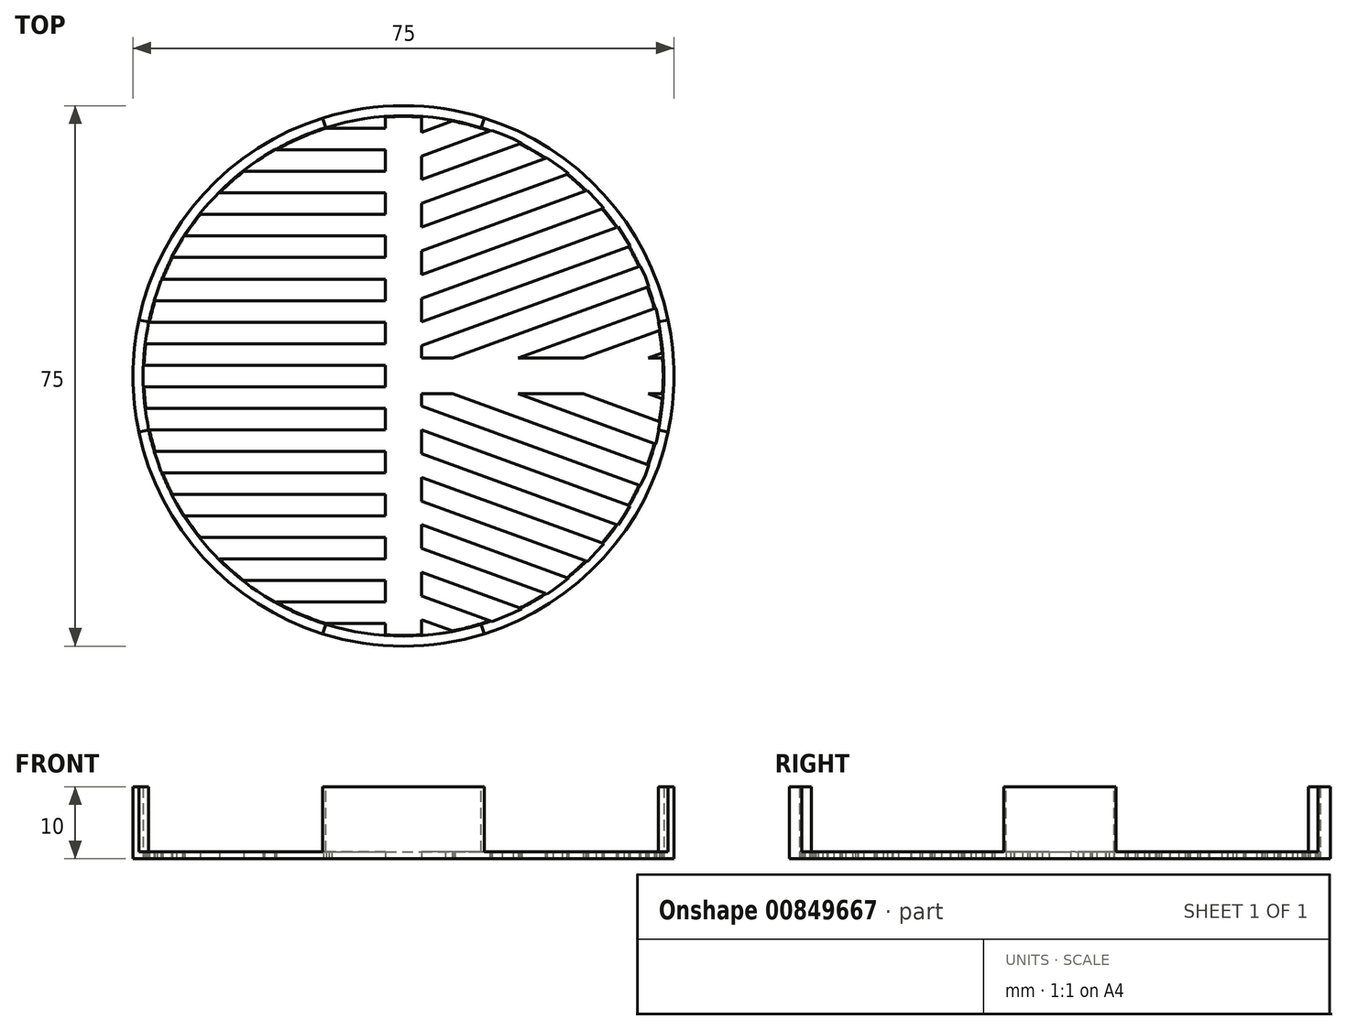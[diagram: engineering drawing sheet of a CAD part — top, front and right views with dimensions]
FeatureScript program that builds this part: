
annotation { "Feature Type Name" : "Feature", "Feature Type Description" : "" }
export const myFeature = defineFeature(function(context is Context, id is Id, definition is map)
    precondition{}
    {
        {
            var Q0;
            Q0=qCreatedBy(makeId("Top.planeOp"),FACE);
            var sketch = newSketch(context, id + "F0", { "sketchPlane" : qUnion([Q0])});
            skLineSegment(sketch, "E0", {"start": v(-11.08, -34.36) * mm, "end": v(-10.31, -34.61) * mm});
            skLineSegment(sketch, "E1", {"start": v(-10.31, -34.61) * mm, "end": v(-7.06, -35.42) * mm});
            skLineSegment(sketch, "E2", {"start": v(-7.06, -35.42) * mm, "end": v(-3.7, -35.92) * mm});
            skLineSegment(sketch, "E3", {"start": v(-3.7, -35.92) * mm, "end": v(-2.5, -36) * mm});
            skLineSegment(sketch, "E4", {"start": v(-2.5, -36) * mm, "end": v(-2.5, -34.36) * mm});
            skLineSegment(sketch, "E5", {"start": v(-2.5, -34.36) * mm, "end": v(-11.08, -34.36) * mm});
            skLineSegment(sketch, "E6", {"start": v(2.5, -33.81) * mm, "end": v(2.5, -36.1) * mm});
            skLineSegment(sketch, "E7", {"start": v(2.5, -36.1) * mm, "end": v(5.83, -35.73) * mm});
            skLineSegment(sketch, "E8", {"start": v(5.83, -35.73) * mm, "end": v(7.1, -35.5) * mm});
            skLineSegment(sketch, "E9", {"start": v(7.1, -35.5) * mm, "end": v(2.5, -33.81) * mm});
            skLineSegment(sketch, "E10", {"start": v(-22.3, -28.39) * mm, "end": v(-21.95, -28.67) * mm});
            skLineSegment(sketch, "E11", {"start": v(-21.95, -28.67) * mm, "end": v(-19.28, -30.53) * mm});
            skLineSegment(sketch, "E12", {"start": v(-19.28, -30.53) * mm, "end": v(-17.88, -31.37) * mm});
            skLineSegment(sketch, "E13", {"start": v(-17.88, -31.37) * mm, "end": v(-2.5, -31.37) * mm});
            skLineSegment(sketch, "E14", {"start": v(-2.5, -31.37) * mm, "end": v(-2.5, -28.39) * mm});
            skLineSegment(sketch, "E15", {"start": v(-2.5, -28.39) * mm, "end": v(-22.3, -28.39) * mm});
            skLineSegment(sketch, "E16", {"start": v(2.5, -27.23) * mm, "end": v(2.5, -30.52) * mm});
            skLineSegment(sketch, "E17", {"start": v(2.5, -30.52) * mm, "end": v(12.26, -34.08) * mm});
            skLineSegment(sketch, "E18", {"start": v(12.26, -34.08) * mm, "end": v(13.7, -33.52) * mm});
            skLineSegment(sketch, "E19", {"start": v(13.7, -33.52) * mm, "end": v(15.18, -32.88) * mm});
            skLineSegment(sketch, "E20", {"start": v(15.18, -32.88) * mm, "end": v(16.4, -32.3) * mm});
            skLineSegment(sketch, "E21", {"start": v(16.4, -32.3) * mm, "end": v(2.5, -27.23) * mm});
            skLineSegment(sketch, "E22", {"start": v(-28.3, -22.41) * mm, "end": v(-27.8, -23.05) * mm});
            skLineSegment(sketch, "E23", {"start": v(-27.8, -23.05) * mm, "end": v(-26.73, -24.28) * mm});
            skLineSegment(sketch, "E24", {"start": v(-26.73, -24.28) * mm, "end": v(-25.66, -25.4) * mm});
            skLineSegment(sketch, "E25", {"start": v(-25.66, -25.4) * mm, "end": v(-2.5, -25.4) * mm});
            skLineSegment(sketch, "E26", {"start": v(-2.5, -25.4) * mm, "end": v(-2.5, -22.41) * mm});
            skLineSegment(sketch, "E27", {"start": v(-2.5, -22.41) * mm, "end": v(-28.3, -22.41) * mm});
            skLineSegment(sketch, "E28", {"start": v(2.5, -20.65) * mm, "end": v(2.5, -23.94) * mm});
            skLineSegment(sketch, "E29", {"start": v(2.5, -23.94) * mm, "end": v(19.88, -30.27) * mm});
            skLineSegment(sketch, "E30", {"start": v(19.88, -30.27) * mm, "end": v(20.74, -29.7) * mm});
            skLineSegment(sketch, "E31", {"start": v(20.74, -29.7) * mm, "end": v(22.02, -28.76) * mm});
            skLineSegment(sketch, "E32", {"start": v(22.02, -28.76) * mm, "end": v(22.88, -28.07) * mm});
            skLineSegment(sketch, "E33", {"start": v(22.88, -28.07) * mm, "end": v(2.5, -20.65) * mm});
            skLineSegment(sketch, "E34", {"start": v(-32.15, -16.43) * mm, "end": v(-31.48, -17.69) * mm});
            skLineSegment(sketch, "E35", {"start": v(-31.48, -17.69) * mm, "end": v(-30.65, -19.1) * mm});
            skLineSegment(sketch, "E36", {"start": v(-30.65, -19.1) * mm, "end": v(-30.43, -19.42) * mm});
            skLineSegment(sketch, "E37", {"start": v(-30.43, -19.42) * mm, "end": v(-2.5, -19.42) * mm});
            skLineSegment(sketch, "E38", {"start": v(-2.5, -19.42) * mm, "end": v(-2.5, -16.43) * mm});
            skLineSegment(sketch, "E39", {"start": v(-2.5, -16.43) * mm, "end": v(-32.15, -16.43) * mm});
            skLineSegment(sketch, "E40", {"start": v(2.5, -14.07) * mm, "end": v(2.5, -17.36) * mm});
            skLineSegment(sketch, "E41", {"start": v(2.5, -17.36) * mm, "end": v(25.49, -25.73) * mm});
            skLineSegment(sketch, "E42", {"start": v(25.49, -25.73) * mm, "end": v(25.61, -25.61) * mm});
            skLineSegment(sketch, "E43", {"start": v(25.61, -25.61) * mm, "end": v(26.7, -24.46) * mm});
            skLineSegment(sketch, "E44", {"start": v(26.7, -24.46) * mm, "end": v(27.76, -23.27) * mm});
            skLineSegment(sketch, "E45", {"start": v(27.76, -23.27) * mm, "end": v(2.5, -14.07) * mm});
            skLineSegment(sketch, "E46", {"start": v(-34.56, -10.46) * mm, "end": v(-34.17, -11.68) * mm});
            skLineSegment(sketch, "E47", {"start": v(-34.17, -11.68) * mm, "end": v(-33.6, -13.24) * mm});
            skLineSegment(sketch, "E48", {"start": v(-33.6, -13.24) * mm, "end": v(-33.51, -13.45) * mm});
            skLineSegment(sketch, "E49", {"start": v(-33.51, -13.45) * mm, "end": v(-2.5, -13.45) * mm});
            skLineSegment(sketch, "E50", {"start": v(-2.5, -13.45) * mm, "end": v(-2.5, -10.46) * mm});
            skLineSegment(sketch, "E51", {"start": v(-2.5, -10.46) * mm, "end": v(-34.56, -10.46) * mm});
            skLineSegment(sketch, "E52", {"start": v(2.5, -7.49) * mm, "end": v(2.5, -10.78) * mm});
            skLineSegment(sketch, "E53", {"start": v(2.5, -10.78) * mm, "end": v(29.73, -20.7) * mm});
            skLineSegment(sketch, "E54", {"start": v(29.73, -20.7) * mm, "end": v(30.58, -19.4) * mm});
            skLineSegment(sketch, "E55", {"start": v(30.58, -19.4) * mm, "end": v(31.4, -18.04) * mm});
            skLineSegment(sketch, "E56", {"start": v(31.4, -18.04) * mm, "end": v(31.42, -18.02) * mm});
            skLineSegment(sketch, "E57", {"start": v(31.42, -18.02) * mm, "end": v(2.5, -7.49) * mm});
            skLineSegment(sketch, "E58", {"start": v(-35.82, -4.48) * mm, "end": v(-35.74, -5.16) * mm});
            skLineSegment(sketch, "E59", {"start": v(-35.74, -5.16) * mm, "end": v(-35.46, -6.83) * mm});
            skLineSegment(sketch, "E60", {"start": v(-35.46, -6.83) * mm, "end": v(-35.32, -7.47) * mm});
            skLineSegment(sketch, "E61", {"start": v(-35.32, -7.47) * mm, "end": v(-2.5, -7.47) * mm});
            skLineSegment(sketch, "E62", {"start": v(-2.5, -7.47) * mm, "end": v(-2.5, -4.48) * mm});
            skLineSegment(sketch, "E63", {"start": v(-2.5, -4.48) * mm, "end": v(-35.82, -4.48) * mm});
            skLineSegment(sketch, "E64", {"start": v(33.96, -2.5) * mm, "end": v(36.04, -3.24) * mm});
            skLineSegment(sketch, "E65", {"start": v(36.04, -3.24) * mm, "end": v(36.1, -2.5) * mm});
            skLineSegment(sketch, "E66", {"start": v(36.1, -2.5) * mm, "end": v(33.96, -2.5) * mm});
            skLineSegment(sketch, "E67", {"start": v(15.88, -2.5) * mm, "end": v(34.95, -9.43) * mm});
            skLineSegment(sketch, "E68", {"start": v(34.95, -9.43) * mm, "end": v(35.06, -9.07) * mm});
            skLineSegment(sketch, "E69", {"start": v(35.06, -9.07) * mm, "end": v(35.43, -7.46) * mm});
            skLineSegment(sketch, "E70", {"start": v(35.43, -7.46) * mm, "end": v(35.62, -6.38) * mm});
            skLineSegment(sketch, "E71", {"start": v(35.62, -6.38) * mm, "end": v(24.92, -2.5) * mm});
            skLineSegment(sketch, "E72", {"start": v(24.92, -2.5) * mm, "end": v(15.88, -2.5) * mm});
            skLineSegment(sketch, "E73", {"start": v(2.5, -2.5) * mm, "end": v(2.5, -4.2) * mm});
            skLineSegment(sketch, "E74", {"start": v(2.5, -4.2) * mm, "end": v(32.85, -15.25) * mm});
            skLineSegment(sketch, "E75", {"start": v(32.85, -15.25) * mm, "end": v(32.88, -15.18) * mm});
            skLineSegment(sketch, "E76", {"start": v(32.88, -15.18) * mm, "end": v(33.52, -13.7) * mm});
            skLineSegment(sketch, "E77", {"start": v(33.52, -13.7) * mm, "end": v(34.03, -12.38) * mm});
            skLineSegment(sketch, "E78", {"start": v(34.03, -12.38) * mm, "end": v(6.84, -2.5) * mm});
            skLineSegment(sketch, "E79", {"start": v(6.84, -2.5) * mm, "end": v(2.5, -2.5) * mm});
            skLineSegment(sketch, "E80", {"start": v(-36.07, 1.5) * mm, "end": v(-36.1, 0) * mm});
            skLineSegment(sketch, "E81", {"start": v(-36.1, 0) * mm, "end": v(-36.07, -1.5) * mm});
            skLineSegment(sketch, "E82", {"start": v(-36.07, -1.5) * mm, "end": v(-2.5, -1.5) * mm});
            skLineSegment(sketch, "E83", {"start": v(-2.5, -1.5) * mm, "end": v(-2.5, 1.5) * mm});
            skLineSegment(sketch, "E84", {"start": v(-2.5, 1.5) * mm, "end": v(-36.07, 1.5) * mm});
            skLineSegment(sketch, "E85", {"start": v(36.04, 3.25) * mm, "end": v(33.96, 2.5) * mm});
            skLineSegment(sketch, "E86", {"start": v(33.96, 2.5) * mm, "end": v(36.1, 2.5) * mm});
            skLineSegment(sketch, "E87", {"start": v(36.1, 2.5) * mm, "end": v(36.04, 3.25) * mm});
            skLineSegment(sketch, "E88", {"start": v(-35.32, 7.47) * mm, "end": v(-35.46, 6.84) * mm});
            skLineSegment(sketch, "E89", {"start": v(-35.46, 6.84) * mm, "end": v(-35.74, 5.16) * mm});
            skLineSegment(sketch, "E90", {"start": v(-35.74, 5.16) * mm, "end": v(-35.82, 4.48) * mm});
            skLineSegment(sketch, "E91", {"start": v(-35.82, 4.48) * mm, "end": v(-2.5, 4.48) * mm});
            skLineSegment(sketch, "E92", {"start": v(-2.5, 4.48) * mm, "end": v(-2.5, 7.47) * mm});
            skLineSegment(sketch, "E93", {"start": v(-2.5, 7.47) * mm, "end": v(-35.32, 7.47) * mm});
            skLineSegment(sketch, "E94", {"start": v(34.95, 9.43) * mm, "end": v(15.88, 2.5) * mm});
            skLineSegment(sketch, "E95", {"start": v(15.88, 2.5) * mm, "end": v(24.92, 2.5) * mm});
            skLineSegment(sketch, "E96", {"start": v(24.92, 2.5) * mm, "end": v(35.62, 6.39) * mm});
            skLineSegment(sketch, "E97", {"start": v(35.62, 6.39) * mm, "end": v(35.43, 7.46) * mm});
            skLineSegment(sketch, "E98", {"start": v(35.43, 7.46) * mm, "end": v(35.06, 9.07) * mm});
            skLineSegment(sketch, "E99", {"start": v(35.06, 9.07) * mm, "end": v(34.95, 9.43) * mm});
            skLineSegment(sketch, "E100", {"start": v(-33.51, 13.45) * mm, "end": v(-33.6, 13.24) * mm});
            skLineSegment(sketch, "E101", {"start": v(-33.6, 13.24) * mm, "end": v(-34.17, 11.68) * mm});
            skLineSegment(sketch, "E102", {"start": v(-34.17, 11.68) * mm, "end": v(-34.56, 10.46) * mm});
            skLineSegment(sketch, "E103", {"start": v(-34.56, 10.46) * mm, "end": v(-2.5, 10.46) * mm});
            skLineSegment(sketch, "E104", {"start": v(-2.5, 10.46) * mm, "end": v(-2.5, 13.45) * mm});
            skLineSegment(sketch, "E105", {"start": v(-2.5, 13.45) * mm, "end": v(-33.51, 13.45) * mm});
            skLineSegment(sketch, "E106", {"start": v(32.85, 15.25) * mm, "end": v(2.5, 4.2) * mm});
            skLineSegment(sketch, "E107", {"start": v(2.5, 4.2) * mm, "end": v(2.5, 2.5) * mm});
            skLineSegment(sketch, "E108", {"start": v(2.5, 2.5) * mm, "end": v(6.84, 2.5) * mm});
            skLineSegment(sketch, "E109", {"start": v(6.84, 2.5) * mm, "end": v(34.03, 12.38) * mm});
            skLineSegment(sketch, "E110", {"start": v(34.03, 12.38) * mm, "end": v(33.52, 13.7) * mm});
            skLineSegment(sketch, "E111", {"start": v(33.52, 13.7) * mm, "end": v(32.88, 15.18) * mm});
            skLineSegment(sketch, "E112", {"start": v(32.88, 15.18) * mm, "end": v(32.85, 15.25) * mm});
            skLineSegment(sketch, "E113", {"start": v(-30.43, 19.42) * mm, "end": v(-30.65, 19.1) * mm});
            skLineSegment(sketch, "E114", {"start": v(-30.65, 19.1) * mm, "end": v(-31.48, 17.69) * mm});
            skLineSegment(sketch, "E115", {"start": v(-31.48, 17.69) * mm, "end": v(-32.15, 16.43) * mm});
            skLineSegment(sketch, "E116", {"start": v(-32.15, 16.43) * mm, "end": v(-2.5, 16.43) * mm});
            skLineSegment(sketch, "E117", {"start": v(-2.5, 16.43) * mm, "end": v(-2.5, 19.42) * mm});
            skLineSegment(sketch, "E118", {"start": v(-2.5, 19.42) * mm, "end": v(-30.43, 19.42) * mm});
            skLineSegment(sketch, "E119", {"start": v(29.73, 20.7) * mm, "end": v(2.5, 10.78) * mm});
            skLineSegment(sketch, "E120", {"start": v(2.5, 10.78) * mm, "end": v(2.5, 7.49) * mm});
            skLineSegment(sketch, "E121", {"start": v(2.5, 7.49) * mm, "end": v(31.42, 18.02) * mm});
            skLineSegment(sketch, "E122", {"start": v(31.42, 18.02) * mm, "end": v(31.4, 18.04) * mm});
            skLineSegment(sketch, "E123", {"start": v(31.4, 18.04) * mm, "end": v(30.58, 19.4) * mm});
            skLineSegment(sketch, "E124", {"start": v(30.58, 19.4) * mm, "end": v(29.73, 20.7) * mm});
            skLineSegment(sketch, "E125", {"start": v(-25.66, 25.4) * mm, "end": v(-26.73, 24.28) * mm});
            skLineSegment(sketch, "E126", {"start": v(-26.73, 24.28) * mm, "end": v(-27.8, 23.05) * mm});
            skLineSegment(sketch, "E127", {"start": v(-27.8, 23.05) * mm, "end": v(-28.3, 22.4) * mm});
            skLineSegment(sketch, "E128", {"start": v(-28.3, 22.4) * mm, "end": v(-2.5, 22.4) * mm});
            skLineSegment(sketch, "E129", {"start": v(-2.5, 22.4) * mm, "end": v(-2.5, 25.4) * mm});
            skLineSegment(sketch, "E130", {"start": v(-2.5, 25.4) * mm, "end": v(-25.66, 25.4) * mm});
            skLineSegment(sketch, "E131", {"start": v(25.49, 25.73) * mm, "end": v(2.5, 17.36) * mm});
            skLineSegment(sketch, "E132", {"start": v(2.5, 17.36) * mm, "end": v(2.5, 14.07) * mm});
            skLineSegment(sketch, "E133", {"start": v(2.5, 14.07) * mm, "end": v(27.76, 23.27) * mm});
            skLineSegment(sketch, "E134", {"start": v(27.76, 23.27) * mm, "end": v(26.7, 24.46) * mm});
            skLineSegment(sketch, "E135", {"start": v(26.7, 24.46) * mm, "end": v(25.61, 25.61) * mm});
            skLineSegment(sketch, "E136", {"start": v(25.61, 25.61) * mm, "end": v(25.49, 25.73) * mm});
            skLineSegment(sketch, "E137", {"start": v(19.88, 30.27) * mm, "end": v(2.5, 23.94) * mm});
            skLineSegment(sketch, "E138", {"start": v(2.5, 23.94) * mm, "end": v(2.5, 20.65) * mm});
            skLineSegment(sketch, "E139", {"start": v(2.5, 20.65) * mm, "end": v(22.88, 28.07) * mm});
            skLineSegment(sketch, "E140", {"start": v(22.88, 28.07) * mm, "end": v(22.02, 28.76) * mm});
            skLineSegment(sketch, "E141", {"start": v(22.02, 28.76) * mm, "end": v(20.74, 29.7) * mm});
            skLineSegment(sketch, "E142", {"start": v(20.74, 29.7) * mm, "end": v(19.88, 30.27) * mm});
            skLineSegment(sketch, "E143", {"start": v(-17.88, 31.37) * mm, "end": v(-19.28, 30.53) * mm});
            skLineSegment(sketch, "E144", {"start": v(-19.28, 30.53) * mm, "end": v(-21.95, 28.67) * mm});
            skLineSegment(sketch, "E145", {"start": v(-21.95, 28.67) * mm, "end": v(-22.3, 28.39) * mm});
            skLineSegment(sketch, "E146", {"start": v(-22.3, 28.39) * mm, "end": v(-2.5, 28.39) * mm});
            skLineSegment(sketch, "E147", {"start": v(-2.5, 28.39) * mm, "end": v(-2.5, 31.37) * mm});
            skLineSegment(sketch, "E148", {"start": v(-2.5, 31.37) * mm, "end": v(-17.88, 31.37) * mm});
            skLineSegment(sketch, "E149", {"start": v(12.26, 34.08) * mm, "end": v(2.5, 30.52) * mm});
            skLineSegment(sketch, "E150", {"start": v(2.5, 30.52) * mm, "end": v(2.5, 27.23) * mm});
            skLineSegment(sketch, "E151", {"start": v(2.5, 27.23) * mm, "end": v(16.4, 32.3) * mm});
            skLineSegment(sketch, "E152", {"start": v(16.4, 32.3) * mm, "end": v(15.18, 32.88) * mm});
            skLineSegment(sketch, "E153", {"start": v(15.18, 32.88) * mm, "end": v(13.7, 33.52) * mm});
            skLineSegment(sketch, "E154", {"start": v(13.7, 33.52) * mm, "end": v(12.26, 34.08) * mm});
            skLineSegment(sketch, "E155", {"start": v(-2.5, 36.01) * mm, "end": v(-3.7, 35.92) * mm});
            skLineSegment(sketch, "E156", {"start": v(-3.7, 35.92) * mm, "end": v(-7.06, 35.42) * mm});
            skLineSegment(sketch, "E157", {"start": v(-7.06, 35.42) * mm, "end": v(-10.31, 34.61) * mm});
            skLineSegment(sketch, "E158", {"start": v(-10.31, 34.61) * mm, "end": v(-11.08, 34.36) * mm});
            skLineSegment(sketch, "E159", {"start": v(-11.08, 34.36) * mm, "end": v(-2.5, 34.36) * mm});
            skLineSegment(sketch, "E160", {"start": v(-2.5, 34.36) * mm, "end": v(-2.5, 36.01) * mm});
            skLineSegment(sketch, "E161", {"start": v(2.5, 36.1) * mm, "end": v(2.5, 33.81) * mm});
            skLineSegment(sketch, "E162", {"start": v(2.5, 33.81) * mm, "end": v(7.1, 35.5) * mm});
            skLineSegment(sketch, "E163", {"start": v(7.1, 35.5) * mm, "end": v(5.83, 35.73) * mm});
            skLineSegment(sketch, "E164", {"start": v(5.83, 35.73) * mm, "end": v(2.5, 36.1) * mm});
            skSolve(sketch);
        }
        {
            var Q0;
            Q0=qCreatedBy(makeId("Top.planeOp"),FACE);
            var sketch = newSketch(context, id + "F1", { "sketchPlane" : qUnion([Q0])});
            skCircle(sketch, "E165", {"center": v(0, 0) * mm, "radius": 37.5 * mm});
            skCircle(sketch, "E166.0", {"center": v(0, 0) * mm, "radius": 36.1 * mm});
            skSolve(sketch);
        }
        {
            var Q0;
            Q0 = qSketchRegion(id + "F1", true);
            extrude(context, id + "F2", {"entities" : qUnion([Q0]), "depth" : 10 * mm, "offsetDistance" : 25 * mm});
        }
        {
            var Q0;
            Q0=qCreatedBy(makeId("Top.planeOp"),FACE);
            var sketch = newSketch(context, id + "F3", { "sketchPlane" : qUnion([Q0])});
            skCircle(sketch, "E167", {"center": v(0, 0) * mm, "radius": 36 * mm});
            skSolve(sketch);
        }
        {
            var Q0;
            Q0 = qSketchRegion(id + "F3", true);
            extrude(context, id + "F4", {"entities" : qUnion([Q0]), "depth" : 1 * mm, "offsetDistance" : 25 * mm});
        }
        {
            var Q0;
            Q0 = qSketchRegion(id + "F0", true);
            extrude(context, id + "F5", {"entities" : qUnion([Q0]), "operationType" : NewBodyOperationType.REMOVE, "depth" : 1 * mm, "offsetDistance" : 25 * mm});
        }
        {
            var Q0;
            Q0=makeQuery(id+"F2.opExtrude","CAP_FACE",FACE,{"disambiguationData":[OSD([sQuery(id+"F1.wireOp",EDGE,"E165"),sQuery(id+"F1.wireOp",EDGE,"E166.0")])],"isStart":false});
            var sketch = newSketch(context, id + "F6", { "sketchPlane" : qUnion([Q0])});
            skArc(sketch, "E168", {"start": v(-35.32, 7.48) * mm, "mid": v(-26.7, 24.3) * mm, "end": v(-10.77, 34.46) * mm});
            skArc(sketch, "E169.0", {"start": v(-36.78, 7.8) * mm, "mid": v(-27.8, 25.3) * mm, "end": v(-11.22, 35.89) * mm});
            skLineSegment(sketch, "E170", {"start": v(-11.22, 35.89) * mm, "end": v(-10.77, 34.46) * mm});
            skLineSegment(sketch, "E171", {"start": v(-36.78, 7.8) * mm, "end": v(-35.32, 7.48) * mm});
            skLineSegment(sketch, "E172.MirrorCS", {"start": v(36.78, 7.8) * mm, "end": v(35.32, 7.48) * mm});
            skLineSegment(sketch, "E173.MirrorCS", {"start": v(11.22, 35.89) * mm, "end": v(10.77, 34.46) * mm});
            skArc(sketch, "E174.MirrorCS", {"start": v(35.32, 7.48) * mm, "mid": v(26.7, 24.3) * mm, "end": v(10.77, 34.46) * mm});
            skArc(sketch, "E175.MirrorCS", {"start": v(36.78, 7.8) * mm, "mid": v(27.8, 25.3) * mm, "end": v(11.22, 35.89) * mm});
            skLineSegment(sketch, "E176.MirrorCS", {"start": v(11.22, -35.89) * mm, "end": v(10.77, -34.46) * mm});
            skLineSegment(sketch, "E177.MirrorCS", {"start": v(36.78, -7.8) * mm, "end": v(35.32, -7.48) * mm});
            skArc(sketch, "E178.MirrorCS", {"start": v(36.78, -7.8) * mm, "mid": v(27.8, -25.3) * mm, "end": v(11.22, -35.89) * mm});
            skArc(sketch, "E179.MirrorCS", {"start": v(35.32, -7.48) * mm, "mid": v(26.7, -24.3) * mm, "end": v(10.77, -34.46) * mm});
            skLineSegment(sketch, "E180.MirrorCS", {"start": v(-36.78, -7.8) * mm, "end": v(-35.32, -7.48) * mm});
            skLineSegment(sketch, "E181.MirrorCS", {"start": v(-11.22, -35.89) * mm, "end": v(-10.77, -34.46) * mm});
            skArc(sketch, "E182.MirrorCS", {"start": v(-35.32, -7.48) * mm, "mid": v(-26.7, -24.3) * mm, "end": v(-10.77, -34.46) * mm});
            skArc(sketch, "E183.MirrorCS", {"start": v(-36.78, -7.8) * mm, "mid": v(-27.8, -25.3) * mm, "end": v(-11.22, -35.89) * mm});
            skSolve(sketch);
        }
        {
            var Q0;
            Q0 = qSketchRegion(id + "F6", true);
            extrude(context, id + "F7", {"entities" : qUnion([Q0]), "operationType" : NewBodyOperationType.REMOVE, "oppositeDirection" : true, "depth" : 9 * mm, "offsetDistance" : 25 * mm});
        }
    });
